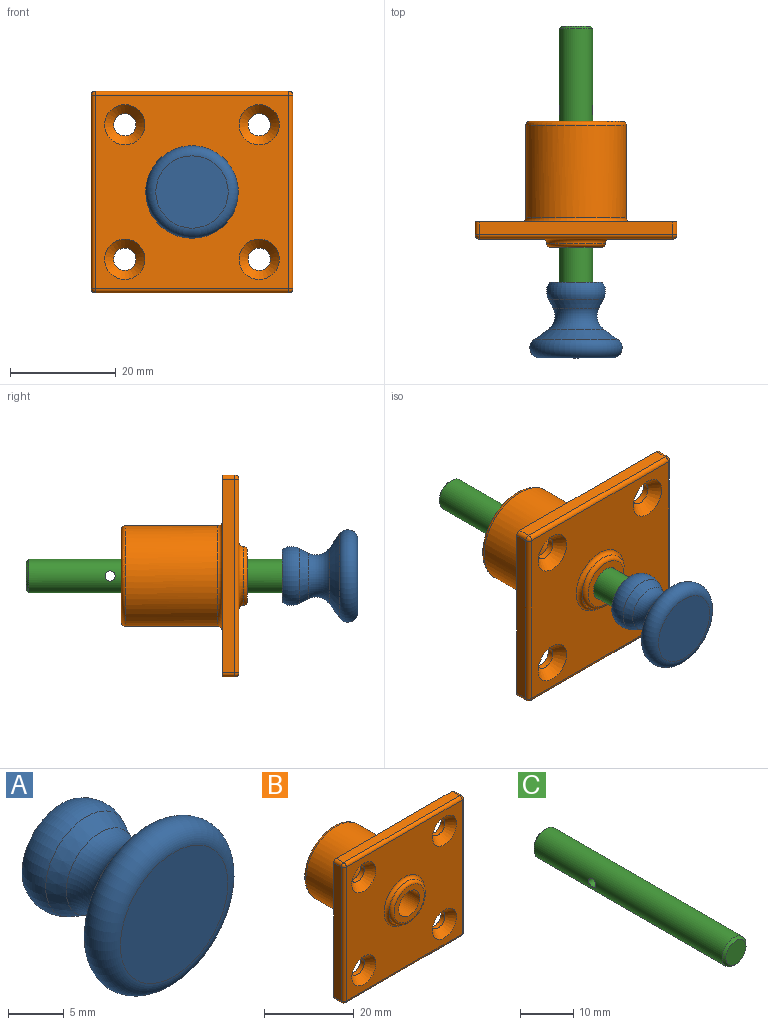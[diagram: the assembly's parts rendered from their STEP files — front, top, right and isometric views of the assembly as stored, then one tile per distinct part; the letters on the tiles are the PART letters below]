
ASSEMBLY  parts=3 mates=2
PART A: 9 faces, bbox 18.9x14.3x18.9 mm
  f0: cylinder r=3.17mm len=6.35mm, axis (0,1,0), area 95mm2, adj f1,f8
  f1: plane 10.1x10.1mm, normal (0,1,0), area 48.4mm2, adj f0,f2
  f2: torus R=2.38mm, axis (0,1,0), area 113mm2, adj f1,f3
  f3: cone r=5.21mm half-angle=27.2deg, axis (0,1,0), area 58.1mm2, adj f2,f4
  f4: torus R=7.14mm, axis (0,1,0), area 122.1mm2, adj f3,f5
  f5: cone r=5.29mm half-angle=54.2deg, axis (0,-1,0), area 135.8mm2, adj f4,f6
  f6: torus R=6.83mm, axis (0,1,0), area 247mm2, adj f5,f7
  f7: plane 13.65x13.65mm, normal (0,-1,0), area 146.4mm2, adj f6
  f8: cone r=3.17mm half-angle=56deg, axis (0,1,0), area 38.2mm2, adj f0
PART B: 36 faces, bbox 38.1x23.8x38.1 mm
  f0: cylinder r=2.11mm len=4.22mm, axis (0,-1,0), area 16.1mm2, adj f1,f13
  f1: cone r=2.11mm half-angle=41deg, axis (0,-1,0), area 48.2mm2, adj f0,f12
  f2: cylinder r=2.11mm len=4.22mm, axis (0,-1,0), area 16.1mm2, adj f3,f13
  f3: cone r=2.11mm half-angle=41deg, axis (0,-1,0), area 48.2mm2, adj f2,f12
  f4: cylinder r=2.11mm len=4.22mm, axis (0,-1,0), area 16.1mm2, adj f5,f13
  f5: cone r=2.11mm half-angle=41deg, axis (0,-1,0), area 48.2mm2, adj f4,f12
  f6: plane 12.7x12.7mm, normal (0,1,0), area 92.4mm2, adj f10,f15
  f7: plane 36.51x2.38mm, normal (0,0,1), area 86.9mm2, adj f13,f26,f32,f35
  f8: plane 36.51x2.38mm, normal (-1,0,0), area 86.9mm2, adj f13,f29,f33,f35
  f9: plane 36.51x2.38mm, normal (0,0,-1), area 86.9mm2, adj f13,f24,f28,f29
  f10: cylinder r=3.3mm len=6.6mm, axis (0,1,0), area 98.8mm2, adj f6,f14
  f11: plane 36.51x2.38mm, normal (1,0,0), area 86.9mm2, adj f13,f24,f26,f27
  f12: plane 36.51x36.51mm, normal (0,-1,0), area 1024.1mm2, adj f1,f3,f5,f19,f23,f27,f28,f32
  f13: plane 38.1x38.1mm, normal (0,1,0), area 1060.7mm2, adj f0,f2,f4,f7,f8,f9,f11,f18
  f14: plane 9.53x9.53mm, normal (0,-1,0), area 37mm2, adj f10,f22
  f15: cylinder r=6.35mm len=19.05mm, axis (0,-1,0), area 760.1mm2, adj f6,f17
  f16: cylinder r=9.53mm len=19.05mm, axis (0,-1,0), area 1045.1mm2, adj f20,f21
  f17: plane 17.46x17.46mm, normal (0,1,0), area 112.8mm2, adj f15,f21
  f18: cylinder r=2.11mm len=4.22mm, axis (0,-1,0), area 16.1mm2, adj f13,f19
  f19: cone r=2.11mm half-angle=41deg, axis (0,-1,0), area 48.2mm2, adj f12,f18
  f20: torus R=10.32mm, axis (0,-1,0), area 76.9mm2, adj f13,f16
  f21: torus R=8.73mm, axis (0,1,0), area 72.4mm2, adj f16,f17
  f22: torus R=4.76mm, axis (0,-1,0), area 41.3mm2, adj f14,f23
  f23: torus R=6.35mm, axis (0,-1,0), area 45.8mm2, adj f12,f22
  f24: cylinder r=0.79mm len=2.38mm, axis (0,-1,0), area 3mm2, adj f9,f11,f13,f25
  f25: sphere r=0.79mm, area 1mm2, adj f24,f27,f28
  f26: cylinder r=0.79mm len=2.38mm, axis (0,1,0), area 3mm2, adj f7,f11,f13,f30
  f27: cylinder r=0.79mm len=36.51mm, axis (0,0,-1), area 45.5mm2, adj f11,f12,f25,f30
  f28: cylinder r=0.79mm len=36.51mm, axis (-1,0,0), area 45.5mm2, adj f9,f12,f25,f31
  f29: cylinder r=0.79mm len=2.38mm, axis (0,1,0), area 3mm2, adj f8,f9,f13,f31
  f30: sphere r=0.79mm, area 1mm2, adj f26,f27,f32
  f31: sphere r=0.79mm, area 1mm2, adj f28,f29,f33
  f32: cylinder r=0.79mm len=36.51mm, axis (1,0,0), area 45.5mm2, adj f7,f12,f30,f34
  f33: cylinder r=0.79mm len=36.51mm, axis (0,0,1), area 45.5mm2, adj f8,f12,f31,f34
  f34: sphere r=0.79mm, area 1mm2, adj f32,f33,f35
  f35: cylinder r=0.79mm len=2.38mm, axis (0,-1,0), area 3mm2, adj f7,f8,f13,f34
PART C: 6 faces, bbox 6.4x50.8x6.4 mm
  f0: cylinder r=3.17mm len=49.78mm, axis (0,1,0), area 987.4mm2, adj f3,f4,f5
  f1: plane 5.33x5.33mm, normal (0,-1,0), area 22.3mm2, adj f4
  f2: plane 5.33x5.33mm, normal (0,1,0), area 22.3mm2, adj f5
  f3: cylinder r=0.95mm len=6.35mm, axis (1,0,0), area 37.1mm2, adj f0
  f4: cone r=2.67mm half-angle=45deg, axis (0,1,0), area 13.2mm2, adj f0,f1
  f5: cone r=3.17mm half-angle=45deg, axis (0,-1,0), area 13.2mm2, adj f0,f2
PLACE A t=(8.38,-11.37,4.89)mm
PLACE B t=(8.38,0,4.89)mm
PLACE C t=(8.38,37.05,4.89)mm
MATE fastened A.f0 <-> C.f0  axis (0,1,0) through (8.38,-13.75,4.89)mm
MATE cylindrical B.f10 <-> A.f0  axis (0,1,0) through (8.38,-4.76,4.89)mm
